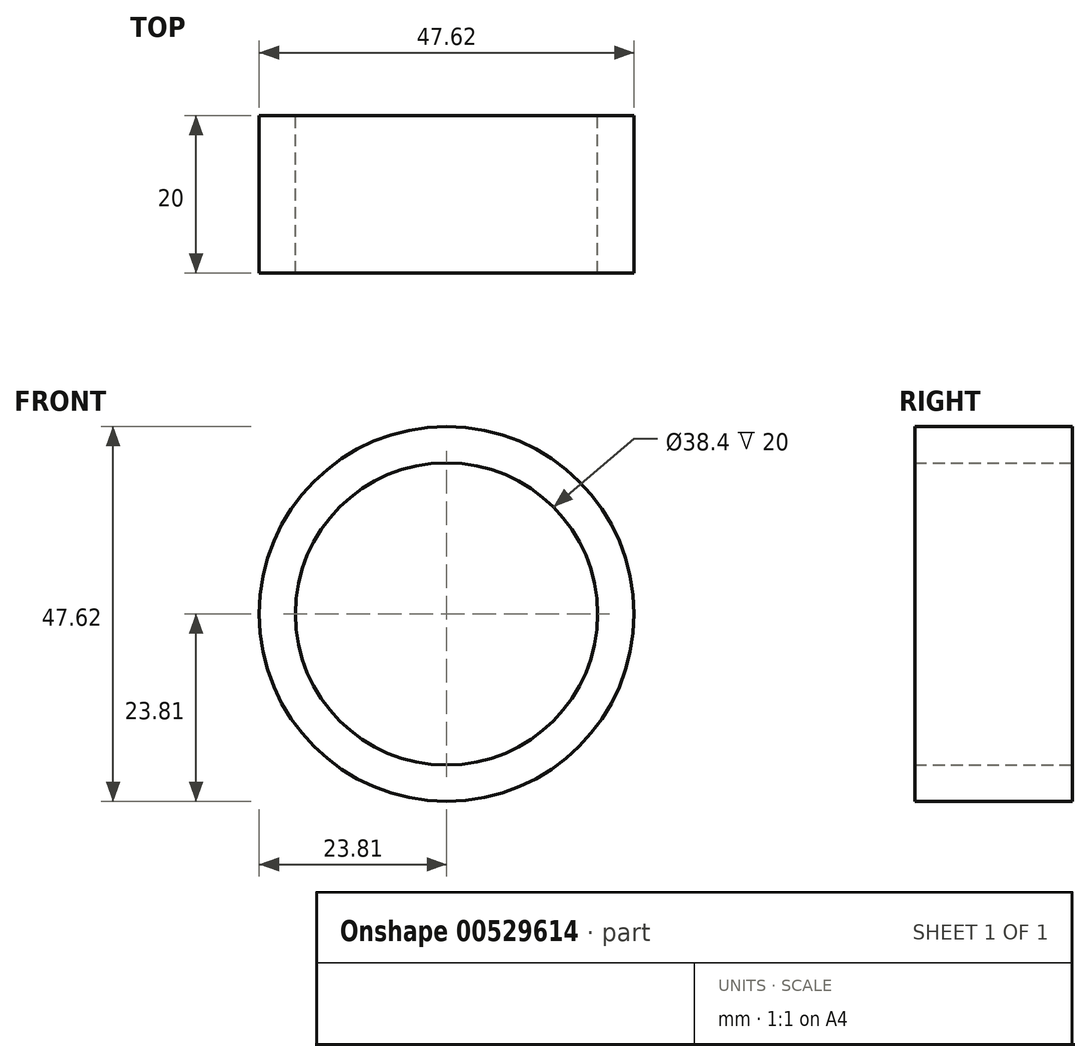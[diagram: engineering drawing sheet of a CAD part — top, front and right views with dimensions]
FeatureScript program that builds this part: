
annotation { "Feature Type Name" : "Feature", "Feature Type Description" : "" }
export const myFeature = defineFeature(function(context is Context, id is Id, definition is map)
    precondition{}
    {
        {
            var Q0;
            Q0=qCreatedBy(makeId("Front.planeOp"),FACE);
            var sketch = newSketch(context, id + "F0", { "sketchPlane" : qUnion([Q0])});
            skCircle(sketch, "E0", {"center": v(0, 0) * mm, "radius": 23.81 * mm});
            skCircle(sketch, "E1", {"center": v(0, 0) * mm, "radius": 19.2 * mm});
            skSolve(sketch);
        }
        {
            var Q0;
            Q0 = qSketchRegion(id + "F0", true);
            extrude(context, id + "F1", {"entities" : qUnion([Q0]), "depth" : 20 * mm, "offsetDistance" : 25 * mm});
        }
    });
